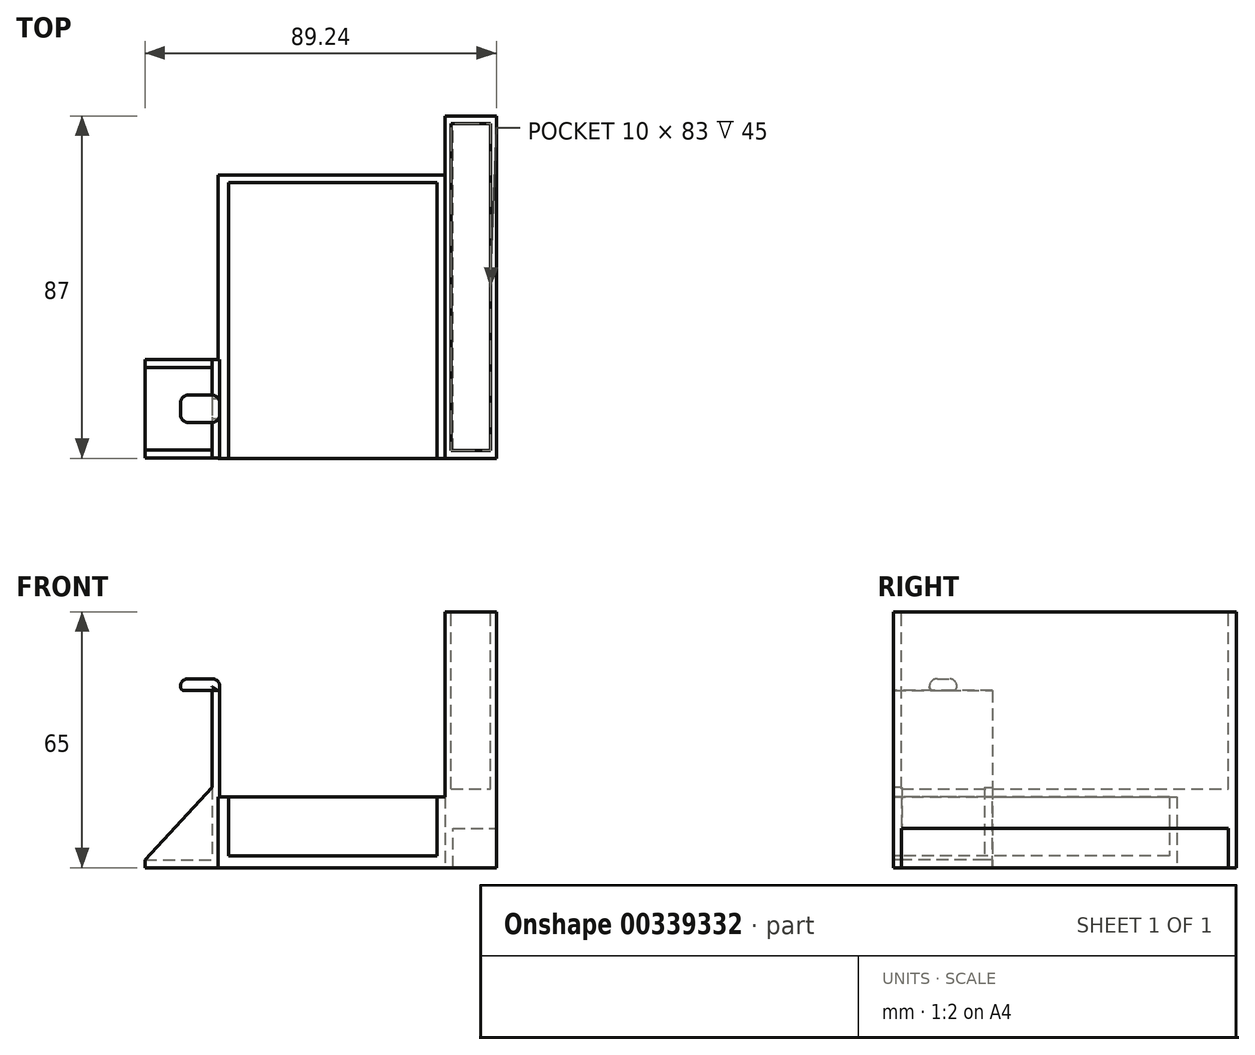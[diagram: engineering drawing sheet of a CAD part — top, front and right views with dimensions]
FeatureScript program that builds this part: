
annotation { "Feature Type Name" : "Feature", "Feature Type Description" : "" }
export const myFeature = defineFeature(function(context is Context, id is Id, definition is map)
    precondition{}
    {
        {
            var Q0;
            Q0=qCreatedBy(makeId("Top.planeOp"),FACE);
            var sketch = newSketch(context, id + "F0", { "sketchPlane" : qUnion([Q0])});
            skLineSegment(sketch, "E0.bottom", {"start": v(14.15, -10.63) * mm, "end": v(31.15, -10.63) * mm});
            skLineSegment(sketch, "E0.top", {"start": v(14.15, -35.63) * mm, "end": v(31.15, -35.63) * mm});
            skLineSegment(sketch, "E0.left", {"start": v(14.15, -10.63) * mm, "end": v(14.15, -35.63) * mm});
            skLineSegment(sketch, "E0.right", {"start": v(31.15, -10.63) * mm, "end": v(31.15, -35.63) * mm});
            skLineSegment(sketch, "E1", {"start": v(31.15, -35.63) * mm, "end": v(33.15, -35.63) * mm});
            skLineSegment(sketch, "E2", {"start": v(33.15, -35.63) * mm, "end": v(33.15, -10.63) * mm});
            skLineSegment(sketch, "E3", {"start": v(33.15, -10.63) * mm, "end": v(31.15, -10.63) * mm});
            skSolve(sketch);
        }
        {
            var Q0;
            Q0=makeQuery(id+"F0.imprint","IMPRINT",FACE,{"disambiguationData":[TD([[makeQuery(id+"F0.imprint","IMPRINT",EDGE,{"derivedFrom":sQuery(id+"F0.wireOp",EDGE,"E0.bottom")}),-1.0]])]});
            var Q1;
            Q1=makeQuery(id+"F0.imprint","IMPRINT",FACE,{"disambiguationData":[TD([[makeQuery(id+"F0.imprint","IMPRINT",EDGE,{"derivedFrom":sQuery(id+"F0.wireOp",EDGE,"E0.bottom")}),-1.0]])]});
            extrude(context, id + "F1", {"entities" : qUnion([Q0, Q1]), "depth" : 2 * mm});
        }
        {
            var Q0;
            Q0=makeQuery(id+"F0.imprint","IMPRINT",FACE,{"disambiguationData":[TD([[makeQuery(id+"F0.imprint","IMPRINT",EDGE,{"derivedFrom":sQuery(id+"F0.wireOp",EDGE,"E0.right")}),1.0]])]});
            extrude(context, id + "F2", {"entities" : qUnion([Q0]), "operationType" : NewBodyOperationType.ADD, "depth" : 45 * mm});
        }
        {
            var Q0;
            Q0=makeQuery(id+"F2.opExtrude","CAP_FACE",FACE,{"disambiguationData":[OSD([sQuery(id+"F0.wireOp",EDGE,"E0.right"),sQuery(id+"F0.wireOp",EDGE,"E1"),sQuery(id+"F0.wireOp",EDGE,"E2"),sQuery(id+"F0.wireOp",EDGE,"E3")])],"isStart":false});
            var sketch = newSketch(context, id + "F3", { "sketchPlane" : qUnion([Q0])});
            skLineSegment(sketch, "E4.bottom", {"start": v(33.15, -26.63) * mm, "end": v(29.15, -26.63) * mm});
            skLineSegment(sketch, "E4.top", {"start": v(33.15, -19.63) * mm, "end": v(23.15, -19.63) * mm});
            skLineSegment(sketch, "E4.left", {"start": v(33.15, -26.63) * mm, "end": v(33.15, -19.63) * mm});
            skLineSegment(sketch, "E4.right", {"start": v(23.15, -25.58) * mm, "end": v(23.15, -19.63) * mm});
            skPoint(sketch, "E4.middle", {"position": v(31.15, -23.13) * mm});
            skLineSegment(sketch, "E5", {"start": v(29.15, -26.63) * mm, "end": v(23.15, -26.63) * mm});
            skLineSegment(sketch, "E6", {"start": v(23.15, -26.63) * mm, "end": v(23.15, -25.58) * mm});
            skSolve(sketch);
        }
        {
            var Q0;
            {var subQ0=sQuery(id+"F3.wireOp",EDGE,"E4.right");Q0=makeQuery(id+"F3.imprint","IMPRINT",FACE,{"disambiguationData":[TD([[makeQuery(id+"F3.imprint","IMPRINT",EDGE,{"derivedFrom":subQ0}),-1.0]])]});}
            var Q1;
            {var subQ0=sQuery(id+"F3.wireOp",EDGE,"E4.left");Q1=makeQuery(id+"F3.imprint","IMPRINT",FACE,{"disambiguationData":[TD([[makeQuery(id+"F3.imprint","IMPRINT",EDGE,{"derivedFrom":subQ0}),1.0]])]});}
            extrude(context, id + "F4", {"entities" : qUnion([Q0, Q1]), "operationType" : NewBodyOperationType.ADD, "depth" : 3 * mm});
        }
        {
            var Q0;
            Q0=makeQuery(id+"F4.opExtrude","CAP_EDGE",EDGE,{"disambiguationData":[OSD([sQuery(id+"F3.wireOp",EDGE,"E4.right"),sQuery(id+"F3.wireOp",EDGE,"E6")])],"isStart":false});
            fillet(context, id + "F5", {"entities" : qUnion([Q0]), "radius" : 2 * mm, "tangentPropagation" : true, "allowEdgeOverflow" : false});
        }
        {
            var Q0;
            Q0=makeQuery(id+"F4.opExtrude","CAP_EDGE",EDGE,{"disambiguationData":[OSD([sQuery(id+"F3.wireOp",EDGE,"E4.bottom"),sQuery(id+"F3.wireOp",EDGE,"E5")])],"isStart":false});
            fillet(context, id + "F6", {"entities" : qUnion([Q0]), "radius" : 2 * mm, "tangentPropagation" : true, "allowEdgeOverflow" : false});
        }
        {
            var Q0;
            Q0=makeQuery(id+"F4.opExtrude","CAP_EDGE",EDGE,{"disambiguationData":[OSD([sQuery(id+"F3.wireOp",EDGE,"E4.top")])],"isStart":false});
            fillet(context, id + "F7", {"entities" : qUnion([Q0]), "radius" : 2 * mm, "tangentPropagation" : true, "allowEdgeOverflow" : false});
        }
        {
            var Q0;
            Q0=makeQuery(id+"F4.opExtrude","CAP_EDGE",EDGE,{"disambiguationData":[OSD([sQuery(id+"F3.wireOp",EDGE,"E4.left")])],"isStart":false});
            fillet(context, id + "F8", {"entities" : qUnion([Q0]), "radius" : 2 * mm, "tangentPropagation" : true, "allowEdgeOverflow" : false});
        }
        {
            var Q0;
            Q0=makeQuery(id+"F4.opExtrude","CAP_EDGE",EDGE,{"disambiguationData":[OSD([sQuery(id+"F3.wireOp",EDGE,"E4.right"),sQuery(id+"F3.wireOp",EDGE,"E6")])],"isStart":true});
            fillet(context, id + "F9", {"entities" : qUnion([Q0]), "radius" : 1 * mm, "tangentPropagation" : true, "allowEdgeOverflow" : false});
        }
        {
            var Q0;
            Q0=makeQuery(id+"F2.boolean.opBoolean","MERGE",FACE,{"derivedFrom":[makeQuery(id+"F1.opExtrude","SWEPT_FACE",FACE,{"disambiguationData":[OSD([sQuery(id+"F0.wireOp",EDGE,"E0.bottom")])]}),makeQuery(id+"F2.opExtrude","SWEPT_FACE",FACE,{"disambiguationData":[OSD([sQuery(id+"F0.wireOp",EDGE,"E3")])]})]});
            var sketch = newSketch(context, id + "F10", { "sketchPlane" : qUnion([Q0])});
            skLineSegment(sketch, "E7", {"start": v(-33.15, 22.5) * mm, "end": v(-14.15, 2) * mm});
            skSolve(sketch);
        }
        {
            var Q0;
            Q0=makeQuery(id+"F2.boolean.opBoolean","MERGE",FACE,{"derivedFrom":[makeQuery(id+"F1.opExtrude","SWEPT_FACE",FACE,{"disambiguationData":[OSD([sQuery(id+"F0.wireOp",EDGE,"E0.top")])]}),makeQuery(id+"F2.opExtrude","SWEPT_FACE",FACE,{"disambiguationData":[OSD([sQuery(id+"F0.wireOp",EDGE,"E1")])]})]});
            var sketch = newSketch(context, id + "F11", { "sketchPlane" : qUnion([Q0])});
            skLineSegment(sketch, "E8", {"start": v(33.15, 22.5) * mm, "end": v(14.15, 2) * mm});
            skSolve(sketch);
        }
        {
            var Q0;
            Q0 = qSketchRegion(id + "F11", true);
            var Q1;
            {var subQ1=sQuery(id+"F0.wireOp",EDGE,"E0.top");var subQ2=makeQuery(id+"F1.opExtrude","CAP_EDGE",EDGE,{"disambiguationData":[OSD([subQ1])],"isStart":false});Q1=makeQuery(id+"F11.imprint","IMPRINT",FACE,{"disambiguationData":[TD([[makeQuery(id+"F11.imprint","IMPRINT",EDGE,{"derivedFrom":subQ2}),1.0]])]});}
            extrude(context, id + "F12", {"entities" : qUnion([Q0, Q1]), "operationType" : NewBodyOperationType.ADD, "oppositeDirection" : true, "depth" : 2 * mm});
        }
        {
            var Q0;
            {var subQ1=sQuery(id+"F0.wireOp",EDGE,"E0.bottom");var subQ2=makeQuery(id+"F1.opExtrude","CAP_EDGE",EDGE,{"disambiguationData":[OSD([subQ1])],"isStart":false});Q0=makeQuery(id+"F10.imprint","IMPRINT",FACE,{"disambiguationData":[TD([[makeQuery(id+"F10.imprint","IMPRINT",EDGE,{"derivedFrom":subQ2}),-1.0]])]});}
            extrude(context, id + "F13", {"entities" : qUnion([Q0]), "operationType" : NewBodyOperationType.ADD, "oppositeDirection" : true, "depth" : 2 * mm});
        }
        {
            var Q0;
            Q0=qCreatedBy(makeId("Top.planeOp"),FACE);
            var sketch = newSketch(context, id + "F14", { "sketchPlane" : qUnion([Q0])});
            skLineSegment(sketch, "E9.bottom", {"start": v(33.4, -35.7) * mm, "end": v(90.4, -35.7) * mm});
            skLineSegment(sketch, "E9.top", {"start": v(33.4, 36.3) * mm, "end": v(90.4, 36.3) * mm});
            skLineSegment(sketch, "E9.left", {"start": v(33.4, -35.7) * mm, "end": v(33.4, 36.3) * mm});
            skLineSegment(sketch, "E9.right", {"start": v(90.4, -35.7) * mm, "end": v(90.4, 36.3) * mm});
            skLineSegment(sketch, "E10.bottom", {"start": v(35.4, 34.3) * mm, "end": v(88.4, 34.3) * mm});
            skLineSegment(sketch, "E10.top", {"start": v(35.4, -33.7) * mm, "end": v(88.4, -33.7) * mm});
            skLineSegment(sketch, "E10.left", {"start": v(35.4, 34.3) * mm, "end": v(35.4, -33.7) * mm});
            skLineSegment(sketch, "E10.right", {"start": v(88.4, 34.3) * mm, "end": v(88.4, -33.7) * mm});
            skSolve(sketch);
        }
        {
            var Q0;
            Q0=makeQuery(id+"F14.imprint","IMPRINT",FACE,{"disambiguationData":[TD([[makeQuery(id+"F14.imprint","IMPRINT",EDGE,{"derivedFrom":sQuery(id+"F14.wireOp",EDGE,"E10.bottom")}),-1.0]])]});
            extrude(context, id + "F15", {"entities" : qUnion([Q0]), "depth" : 3 * mm});
        }
        {
            var Q0;
            Q0=makeQuery(id+"F14.imprint","IMPRINT",FACE,{"disambiguationData":[TD([[makeQuery(id+"F14.imprint","IMPRINT",EDGE,{"derivedFrom":sQuery(id+"F14.wireOp",EDGE,"E9.bottom")}),1.0]])]});
            extrude(context, id + "F16", {"entities" : qUnion([Q0]), "operationType" : NewBodyOperationType.ADD, "depth" : 23 * mm});
        }
        {
            var Q0;
            Q0=makeQuery(id+"F16.opExtrude","CAP_FACE",FACE,{"disambiguationData":[OSD([sQuery(id+"F14.wireOp",EDGE,"E9.bottom"),sQuery(id+"F14.wireOp",EDGE,"E9.top"),sQuery(id+"F14.wireOp",EDGE,"E9.left"),sQuery(id+"F14.wireOp",EDGE,"E9.right"),sQuery(id+"F14.wireOp",EDGE,"E10.bottom"),sQuery(id+"F14.wireOp",EDGE,"E10.top"),sQuery(id+"F14.wireOp",EDGE,"E10.left"),sQuery(id+"F14.wireOp",EDGE,"E10.right")])],"isStart":false});
            var sketch = newSketch(context, id + "F17", { "sketchPlane" : qUnion([Q0])});
            skLineSegment(sketch, "E11.bottom", {"start": v(35.4, -33.7) * mm, "end": v(88.36, -33.7) * mm});
            skLineSegment(sketch, "E11.top", {"start": v(35.4, -35.7) * mm, "end": v(88.36, -35.7) * mm});
            skLineSegment(sketch, "E11.left", {"start": v(35.4, -33.7) * mm, "end": v(35.4, -35.7) * mm});
            skLineSegment(sketch, "E11.right", {"start": v(88.36, -33.7) * mm, "end": v(88.36, -35.7) * mm});
            skSolve(sketch);
        }
        {
            var Q0;
            Q0 = qSketchRegion(id + "F17", true);
            extrude(context, id + "F18", {"entities" : qUnion([Q0]), "operationType" : NewBodyOperationType.REMOVE, "oppositeDirection" : true, "depth" : 20 * mm});
        }
        {
            var Q0;
            Q0=makeQuery(id+"F16.opExtrude","SWEPT_FACE",FACE,{"disambiguationData":[OSD([sQuery(id+"F14.wireOp",EDGE,"E9.left")])]});
            extrude(context, id + "F19", {"entities" : qUnion([Q0]), "depth" : 0.7 * mm});
        }
        {
            var Q0;
            Q0=makeQuery(id+"F1.opExtrude","SWEPT_BODY",BODY,{"disambiguationData":[OSD([sQuery(id+"F0.wireOp",EDGE,"E0.bottom"),sQuery(id+"F0.wireOp",EDGE,"E0.top"),sQuery(id+"F0.wireOp",EDGE,"E0.left"),sQuery(id+"F0.wireOp",EDGE,"E0.right")])]});
            var Q1;
            Q1=makeQuery(id+"F19.opExtrude","SWEPT_BODY",BODY,{"disambiguationData":[OSD([sQuery(id+"F14.wireOp",EDGE,"E9.left")])]});
            var Q2;
            Q2=makeQuery(id+"F15.opExtrude","SWEPT_BODY",BODY,{"disambiguationData":[OSD([sQuery(id+"F14.wireOp",EDGE,"E10.bottom"),sQuery(id+"F14.wireOp",EDGE,"E10.top"),sQuery(id+"F14.wireOp",EDGE,"E10.left"),sQuery(id+"F14.wireOp",EDGE,"E10.right")])]});
            booleanBodies(context, id + "F20", {"operationType" : BooleanOperationType.UNION, "tools" : qUnion([Q0, Q1, Q2])});
        }
        {
            var Q0;
            {var subQ0=sQuery(id+"F14.wireOp",EDGE,"E9.left");Q0=makeQuery(id+"F20.opBoolean","MERGE",FACE,{"derivedFrom":[makeQuery(id+"F16.opExtrude","CAP_FACE",FACE,{"disambiguationData":[OSD([sQuery(id+"F14.wireOp",EDGE,"E9.bottom"),sQuery(id+"F14.wireOp",EDGE,"E9.top"),subQ0,sQuery(id+"F14.wireOp",EDGE,"E9.right"),sQuery(id+"F14.wireOp",EDGE,"E10.bottom"),sQuery(id+"F14.wireOp",EDGE,"E10.top"),sQuery(id+"F14.wireOp",EDGE,"E10.left"),sQuery(id+"F14.wireOp",EDGE,"E10.right")])],"isStart":false}),makeQuery(id+"F19.opExtrude","SWEPT_FACE",FACE,{"disambiguationData":[OSD([subQ0]),TDD([makeQuery(id+"F16.opExtrude","CAP_EDGE",EDGE,{"disambiguationData":[OSD([subQ0])],"isStart":false})])]})]});}
            extrude(context, id + "F21", {"entities" : qUnion([Q0]), "operationType" : NewBodyOperationType.REMOVE, "oppositeDirection" : true, "depth" : 5 * mm});
        }
        {
            var Q0;
            Q0=makeQuery(id+"F16.opExtrude","SWEPT_FACE",FACE,{"disambiguationData":[OSD([sQuery(id+"F14.wireOp",EDGE,"E9.right")])]});
            var sketch = newSketch(context, id + "F22", { "sketchPlane" : qUnion([Q0])});
            skLineSegment(sketch, "E12.bottom", {"start": v(-35.7, 0) * mm, "end": v(51.3, 0) * mm});
            skLineSegment(sketch, "E12.top", {"start": v(-35.7, 65) * mm, "end": v(51.3, 65) * mm});
            skLineSegment(sketch, "E12.left", {"start": v(-35.7, 0) * mm, "end": v(-35.7, 65) * mm});
            skLineSegment(sketch, "E12.right", {"start": v(51.3, 0) * mm, "end": v(51.3, 65) * mm});
            skSolve(sketch);
        }
        {
            var Q0;
            Q0 = qSketchRegion(id + "F22", true);
            extrude(context, id + "F23", {"entities" : qUnion([Q0]), "operationType" : NewBodyOperationType.ADD, "depth" : 13 * mm});
        }
        {
            var Q0;
            Q0=makeQuery(id+"F23.opExtrude","SWEPT_FACE",FACE,{"disambiguationData":[OSD([sQuery(id+"F22.wireOp",EDGE,"E12.top")])]});
            var sketch = newSketch(context, id + "F24", { "sketchPlane" : qUnion([Q0])});
            skLineSegment(sketch, "E13.bottom", {"start": v(91.9, -33.7) * mm, "end": v(101.9, -33.7) * mm});
            skLineSegment(sketch, "E13.top", {"start": v(91.9, 49.3) * mm, "end": v(101.9, 49.3) * mm});
            skLineSegment(sketch, "E13.left", {"start": v(91.9, -33.7) * mm, "end": v(91.9, 49.3) * mm});
            skLineSegment(sketch, "E13.right", {"start": v(101.9, -33.7) * mm, "end": v(101.9, 49.3) * mm});
            skSolve(sketch);
        }
        {
            var Q0;
            Q0=makeQuery(id+"F23.opExtrude","CAP_FACE",FACE,{"disambiguationData":[OSD([sQuery(id+"F22.wireOp",EDGE,"E12.bottom"),sQuery(id+"F22.wireOp",EDGE,"E12.top"),sQuery(id+"F22.wireOp",EDGE,"E12.left"),sQuery(id+"F22.wireOp",EDGE,"E12.right")])],"isStart":false});
            var sketch = newSketch(context, id + "F25", { "sketchPlane" : qUnion([Q0])});
            skLineSegment(sketch, "E14", {"start": v(-35.7, 0) * mm, "end": v(-33.7, 0) * mm});
            skLineSegment(sketch, "E15.bottom", {"start": v(-33.7, 0) * mm, "end": v(49.3, 0) * mm});
            skLineSegment(sketch, "E15.top", {"start": v(-33.7, 10) * mm, "end": v(49.3, 10) * mm});
            skLineSegment(sketch, "E15.left", {"start": v(-33.7, 0) * mm, "end": v(-33.7, 10) * mm});
            skLineSegment(sketch, "E15.right", {"start": v(49.3, 0) * mm, "end": v(49.3, 10) * mm});
            skSolve(sketch);
        }
        {
            var Q0;
            Q0 = qSketchRegion(id + "F25", true);
            extrude(context, id + "F26", {"entities" : qUnion([Q0]), "operationType" : NewBodyOperationType.REMOVE, "oppositeDirection" : true, "depth" : 11 * mm});
        }
        {
            var Q0;
            Q0 = qSketchRegion(id + "F24", true);
            extrude(context, id + "F27", {"entities" : qUnion([Q0]), "operationType" : NewBodyOperationType.ADD, "oppositeDirection" : true, "depth" : 45 * mm});
        }
        {
            var Q0;
            Q0=makeQuery(id+"F24.imprint","IMPRINT",FACE,{"disambiguationData":[TD([[makeQuery(id+"F24.imprint","IMPRINT",EDGE,{"derivedFrom":sQuery(id+"F24.wireOp",EDGE,"E13.bottom")}),1.0]])]});
            extrude(context, id + "F28", {"entities" : qUnion([Q0]), "operationType" : NewBodyOperationType.ADD, "oppositeDirection" : true, "depth" : 45 * mm});
        }
        {
            var Q0;
            Q0 = qSketchRegion(id + "F24", true);
            extrude(context, id + "F29", {"entities" : qUnion([Q0]), "operationType" : NewBodyOperationType.REMOVE, "oppositeDirection" : true, "depth" : 45 * mm});
        }
    });
